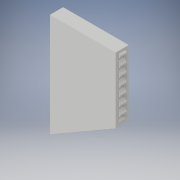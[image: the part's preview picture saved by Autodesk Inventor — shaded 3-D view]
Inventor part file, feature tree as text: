
AUTODESK INVENTOR PART (.ipt)
format: ipt  version: 2017 (Build 210142000, 142)  size: 342,528 bytes
history: native  units: in
note: dims shown in document units (in); Inventor stores cm internally (conversion verified against a paired STEP export)
features: extrude x3, sketch x1
ambient origin geometry x8: Origin, YZ Plane, XZ Plane, XY Plane, X Axis, Y Axis, Z Axis, Center Point
bodies: Solid1 (feature_tree)
feature tree (4):
  extrude  "door"  Depth=1.0in
  sketch  "Sketch3"  dims[d143=10.0in d144=0.0in d282=1.0in d283=1.0in d284=1.5in d285=1.5in d350=1.5in d351=1.0in d352=1.5in d353=0.9496in d356=0.9496in d358=1.0in d359=1.0in d360=1.0in d361=1.5in d362=1.5in d363=1.5in d364=1.0in d365=1.5in d366=0.9496in d367=0.9496in d368=1.0in d369=1.0in d370=1.0in d371=1.5in d372=1.5in d373=1.5in d374=1.0in d375=1.5in d376=0.9496in d377=0.9496in d378=1.0in d379=1.0in d380=1.0in d381=1.5in d382=1.5in d383=1.5in d384=1.0in d385=1.5in d386=0.9496in d387=0.9496in d388=1.0in d389=1.0in d390=1.0in d391=1.5in d392=1.5in d393=1.5in d394=1.0in d395=1.5in d396=0.9496in d397=0.9496in d398=1.0in d399=1.0in d400=1.0in d401=1.5in d402=1.5in d403=1.5in d404=1.0in d405=1.5in d406=0.9496in d407=0.9496in d408=1.0in d409=1.0in d410=1.0in d411=1.5in d412=1.5in d413=1.5in d414=1.0in d415=1.5in d416=0.9496in d417=0.9496in d418=1.0in d419=1.0in d420=1.0in d421=1.5in d422=1.5in d423=1.5in d424=1.0in d425=1.5in d426=0.9496in d427=0.9496in d428=1.0in d429=1.0in d430=1.0in d431=1.5in d432=1.5in d436=0.9496in d439=5.0in d440=0.0in d441=5.0in d442=0.0in d446=78.8675in]
  extrude  "connection give"  Depth=5.0in
  extrude  "connection receive"  Depth=1.0in
